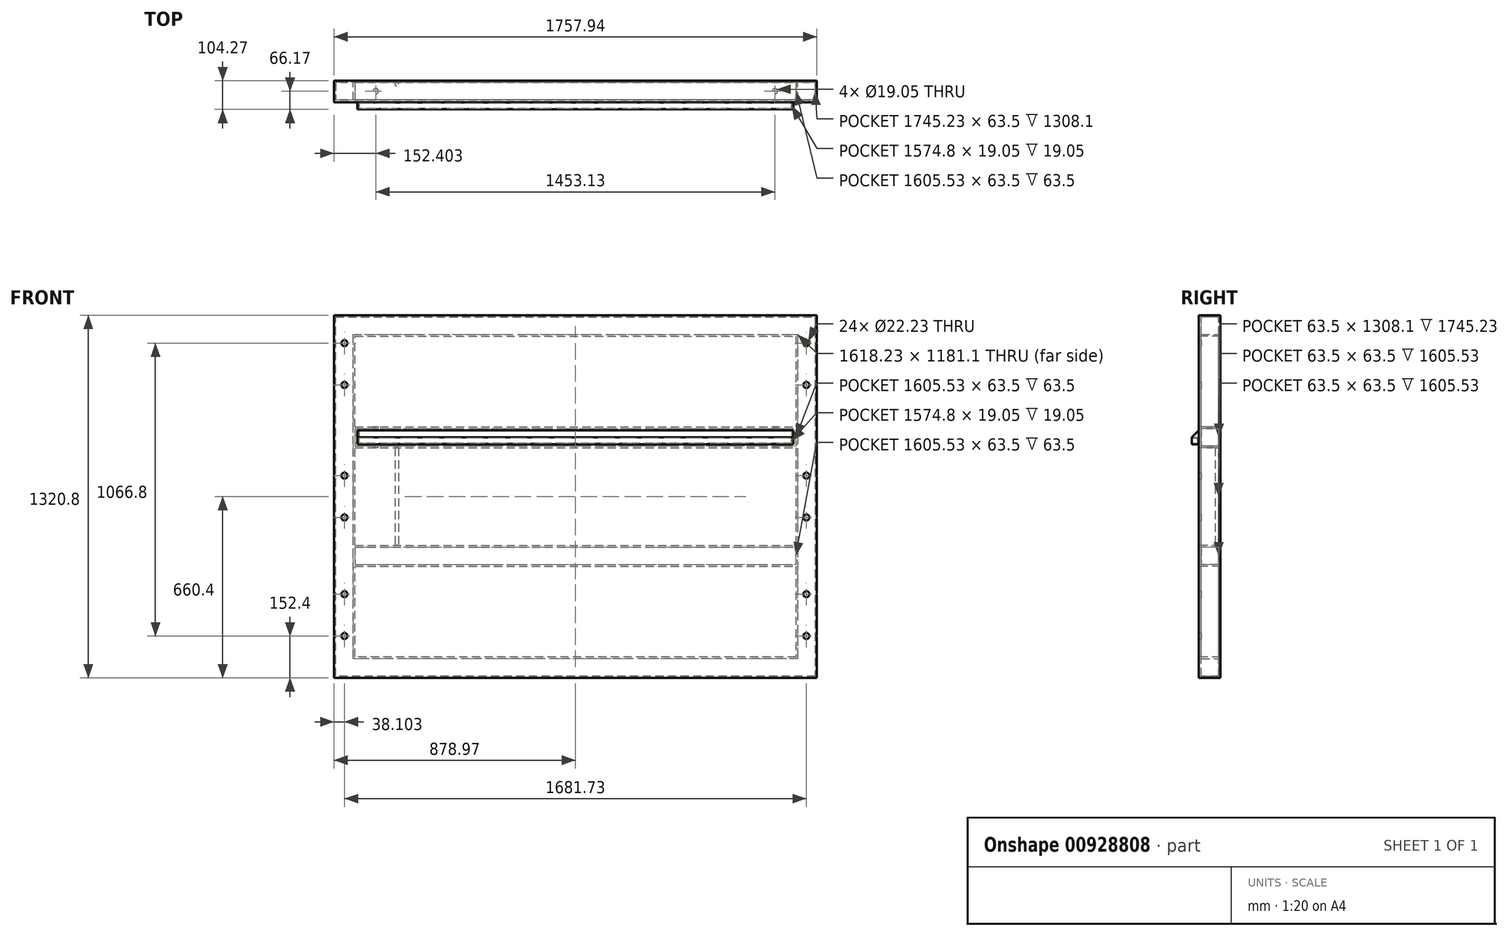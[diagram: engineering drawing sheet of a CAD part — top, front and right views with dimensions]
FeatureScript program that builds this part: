
annotation { "Feature Type Name" : "Feature", "Feature Type Description" : "" }
export const myFeature = defineFeature(function(context is Context, id is Id, definition is map)
    precondition{}
    {
        {
            var Q0;
            Q0=qCreatedBy(makeId("Front.planeOp"),FACE);
            var sketch = newSketch(context, id + "F0", { "sketchPlane" : qUnion([Q0])});
            skLineSegment(sketch, "E0.bottom", {"start": v(-878.97, 660.4) * mm, "end": v(878.97, 660.4) * mm});
            skLineSegment(sketch, "E0.top", {"start": v(-878.97, -660.4) * mm, "end": v(878.97, -660.4) * mm});
            skLineSegment(sketch, "E0.left", {"start": v(-878.97, 660.4) * mm, "end": v(-878.97, -660.4) * mm});
            skLineSegment(sketch, "E0.right", {"start": v(878.97, 660.4) * mm, "end": v(878.97, -660.4) * mm});
            skLineSegment(sketch, "E1.bottom", {"start": v(-802.77, 635) * mm, "end": v(802.77, 635) * mm, "construction": true});
            skLineSegment(sketch, "E1.top", {"start": v(-802.77, -609.6) * mm, "end": v(802.77, -609.6) * mm, "construction": true});
            skLineSegment(sketch, "E1.left", {"start": v(-802.77, 635) * mm, "end": v(-802.77, -609.6) * mm, "construction": true});
            skLineSegment(sketch, "E1.right", {"start": v(802.77, 635) * mm, "end": v(802.77, -609.6) * mm, "construction": true});
            skLineSegment(sketch, "E2", {"start": v(0, 0) * mm, "end": v(0, 635) * mm, "construction": true});
            skSolve(sketch);
        }
        {
            var Q0;
            Q0=qCreatedBy(makeId("Top.planeOp"),FACE);
            var sketch = newSketch(context, id + "F1", { "sketchPlane" : qUnion([Q0])});
            skLineSegment(sketch, "E3.bottom", {"start": v(-802.77, -76.2) * mm, "end": v(-878.97, -76.2) * mm});
            skLineSegment(sketch, "E3.top", {"start": v(-802.77, 0) * mm, "end": v(-878.97, 0) * mm});
            skLineSegment(sketch, "E3.left", {"start": v(-802.77, -76.2) * mm, "end": v(-802.77, 0) * mm});
            skLineSegment(sketch, "E3.right", {"start": v(-878.97, -76.2) * mm, "end": v(-878.97, 0) * mm});
            skPoint(sketch, "E3.middle", {"position": v(-840.87, -38.1) * mm});
            skLineSegment(sketch, "E4.bottom", {"start": v(-809.12, -69.85) * mm, "end": v(-872.62, -69.85) * mm});
            skLineSegment(sketch, "E4.top", {"start": v(-809.12, -6.35) * mm, "end": v(-872.62, -6.35) * mm});
            skLineSegment(sketch, "E4.left", {"start": v(-809.12, -69.85) * mm, "end": v(-809.12, -6.35) * mm});
            skLineSegment(sketch, "E4.right", {"start": v(-872.62, -69.85) * mm, "end": v(-872.62, -6.35) * mm});
            skSolve(sketch);
        }
        {
            var Q0;
            Q0=qSketchRegion(id+"F1",true);
            var Q1;
            Q1=qConstructionFilter(qBodyType(qCreatedBy(id+"F0",EDGE),BodyType.WIRE),ConstructionObject.NO);
            sweep(context, id + "F2", {"profiles" : qUnion([Q0]), "path" : qUnion([Q1])});
        }
        {
            var Q0;
            Q0=qCreatedBy(makeId("Right.planeOp"),FACE);
            var sketch = newSketch(context, id + "F3", { "sketchPlane" : qUnion([Q0])});
            skLineSegment(sketch, "E5.bottom", {"start": v(0, 660.4) * mm, "end": v(-76.2, 660.4) * mm, "construction": true});
            skLineSegment(sketch, "E5.top", {"start": v(0, 584.2) * mm, "end": v(-76.2, 584.2) * mm, "construction": true});
            skLineSegment(sketch, "E5.left", {"start": v(0, 660.4) * mm, "end": v(0, 584.2) * mm, "construction": true});
            skLineSegment(sketch, "E5.right", {"start": v(-76.2, 660.4) * mm, "end": v(-76.2, 584.2) * mm, "construction": true});
            skPoint(sketch, "E5.middle", {"position": v(-38.1, 622.3) * mm});
            skLineSegment(sketch, "E6.bottom", {"start": v(-6.35, 654.05) * mm, "end": v(-69.85, 654.05) * mm, "construction": true});
            skLineSegment(sketch, "E6.top", {"start": v(-6.35, 590.55) * mm, "end": v(-69.85, 590.55) * mm, "construction": true});
            skLineSegment(sketch, "E6.left", {"start": v(-6.35, 654.05) * mm, "end": v(-6.35, 590.55) * mm, "construction": true});
            skLineSegment(sketch, "E6.right", {"start": v(-69.85, 654.05) * mm, "end": v(-69.85, 590.55) * mm, "construction": true});
            skLineSegment(sketch, "E7.0.1.0", {"start": v(0, 254) * mm, "end": v(-76.2, 254) * mm});
            skLineSegment(sketch, "E7.0.1.1", {"start": v(0, 177.8) * mm, "end": v(-76.2, 177.8) * mm});
            skLineSegment(sketch, "E7.0.1.2", {"start": v(0, 254) * mm, "end": v(0, 177.8) * mm});
            skLineSegment(sketch, "E7.0.1.3", {"start": v(-76.2, 254) * mm, "end": v(-76.2, 177.8) * mm});
            skLineSegment(sketch, "E7.0.1.4", {"start": v(-6.35, 247.65) * mm, "end": v(-69.85, 247.65) * mm});
            skLineSegment(sketch, "E7.0.1.5", {"start": v(-6.35, 184.15) * mm, "end": v(-69.85, 184.15) * mm});
            skLineSegment(sketch, "E7.0.1.6", {"start": v(-6.35, 247.65) * mm, "end": v(-6.35, 184.15) * mm});
            skLineSegment(sketch, "E7.0.1.7", {"start": v(-69.85, 247.65) * mm, "end": v(-69.85, 184.15) * mm});
            skLineSegment(sketch, "E7.direction1", {"start": v(-76.2, 584.2) * mm, "end": v(586.54, 584.2) * mm, "construction": true});
            skLineSegment(sketch, "E8.0.0.2", {"start": v(0, -177.8) * mm, "end": v(-76.2, -177.8) * mm});
            skLineSegment(sketch, "E8.3.0.2", {"start": v(0, -254) * mm, "end": v(-76.2, -254) * mm});
            skLineSegment(sketch, "E8.6.0.2", {"start": v(0, -177.8) * mm, "end": v(0, -254) * mm});
            skLineSegment(sketch, "E8.9.0.2", {"start": v(-76.2, -177.8) * mm, "end": v(-76.2, -254) * mm});
            skLineSegment(sketch, "E8.12.0.2", {"start": v(-6.35, -184.15) * mm, "end": v(-69.85, -184.15) * mm});
            skLineSegment(sketch, "E8.15.0.2", {"start": v(-6.35, -247.65) * mm, "end": v(-69.85, -247.65) * mm});
            skLineSegment(sketch, "E8.18.0.2", {"start": v(-6.35, -184.15) * mm, "end": v(-6.35, -247.65) * mm});
            skLineSegment(sketch, "E8.21.0.2", {"start": v(-69.85, -184.15) * mm, "end": v(-69.85, -247.65) * mm});
            skLineSegment(sketch, "E9", {"start": v(-38.1, 584.2) * mm, "end": v(-38.1, 254) * mm, "construction": true});
            skLineSegment(sketch, "E10", {"start": v(-38.1, 177.8) * mm, "end": v(-38.1, -177.8) * mm, "construction": true});
            skLineSegment(sketch, "E11", {"start": v(-38.1, -254) * mm, "end": v(-38.1, -584.2) * mm, "construction": true});
            skLineSegment(sketch, "E12", {"start": v(-38.1, 254) * mm, "end": v(-38.1, 247.65) * mm, "construction": true});
            skLineSegment(sketch, "E13", {"start": v(-69.85, 215.9) * mm, "end": v(-76.2, 215.9) * mm, "construction": true});
            skPoint(sketch, "E13.endSnap0", {"position": v(-76.2, 215.9) * mm});
            skLineSegment(sketch, "E14", {"start": v(-38.1, -254) * mm, "end": v(-38.1, -247.65) * mm, "construction": true});
            skLineSegment(sketch, "E15", {"start": v(-69.85, -215.9) * mm, "end": v(-76.2, -215.9) * mm, "construction": true});
            skSolve(sketch);
        }
        {
            var Q0;
            Q0=qSketchRegion(id+"F3",true);
            var Q1;
            Q1=makeQuery(id+"F2.opSweep","SWEPT_FACE",FACE,{"disambiguationData":[OSD([sQuery(id+"F0.wireOp",EDGE,"E0.left"),sQuery(id+"F1.wireOp",EDGE,"E3.left")])]});
            var Q2;
            Q2=makeQuery(id+"F2.opSweep","CAP_VERTEX",VERTEX,{"disambiguationData":[OSD([sQuery(id+"F0.wireOp",EDGE,"E0.bottom"),sQuery(id+"F1.wireOp",EDGE,"E3.bottom"),sQuery(id+"F1.wireOp",EDGE,"E3.left")])],"isStart":true});
            var Q3;
            Q3=makeQuery(id+"F2.opSweep","SWEPT_FACE",FACE,{"disambiguationData":[OSD([sQuery(id+"F0.wireOp",EDGE,"E0.right"),sQuery(id+"F1.wireOp",EDGE,"E3.left")])]});
            var Q4;
            Q4=makeQuery(id+"F2.opSweep","MID_CAP_VERTEX",VERTEX,{"disambiguationData":[OSD([sQuery(id+"F0.wireOp",EDGE,"E0.bottom"),sQuery(id+"F1.wireOp",EDGE,"E3.bottom"),sQuery(id+"F1.wireOp",EDGE,"E3.left")])],"capPos":1.0});
            extrude(context, id + "F4", {"entities" : qUnion([Q0]), "operationType" : NewBodyOperationType.ADD, "endBound" : BoundingType.UP_TO_VERTEX, "oppositeDirection" : true, "depth" : 25.4 * mm, "endBoundEntityFace" : qUnion([Q1]), "endBoundEntityVertex" : qUnion([Q2]), "offsetDistance" : 25.4 * mm, "hasSecondDirection" : true, "secondDirectionBound" : SecondDirectionBoundingType.UP_TO_VERTEX, "secondDirectionOppositeDirection" : false, "secondDirectionDepth" : 25.4 * mm, "secondDirectionBoundEntityFace" : qUnion([Q3]), "secondDirectionBoundEntityVertex" : qUnion([Q4])});
        }
        {
            var Q0;
            Q0=qCreatedBy(makeId("Top.planeOp"),FACE);
            var sketch = newSketch(context, id + "F5", { "sketchPlane" : qUnion([Q0])});
            skLineSegment(sketch, "E16.bottom", {"start": v(878.97, -78.87) * mm, "end": v(-878.97, -78.87) * mm});
            skLineSegment(sketch, "E16.top", {"start": v(878.97, -76.2) * mm, "end": v(-878.97, -76.2) * mm});
            skLineSegment(sketch, "E16.left", {"start": v(878.97, -78.87) * mm, "end": v(878.97, -76.2) * mm});
            skLineSegment(sketch, "E16.right", {"start": v(-878.97, -78.87) * mm, "end": v(-878.97, -76.2) * mm});
            skPoint(sketch, "E16.middle", {"position": v(0, -77.53) * mm});
            skSolve(sketch);
        }
        {
            var Q0;
            Q0=qSketchRegion(id+"F5",true);
            var Q1;
            Q1=makeQuery(id+"F2.opSweep","CAP_VERTEX",VERTEX,{"disambiguationData":[OSD([sQuery(id+"F0.wireOp",EDGE,"E0.bottom"),sQuery(id+"F1.wireOp",EDGE,"E3.bottom"),sQuery(id+"F1.wireOp",EDGE,"E3.right")])],"isStart":true});
            var Q2;
            Q2=makeQuery(id+"F2.opSweep","MID_CAP_VERTEX",VERTEX,{"disambiguationData":[OSD([sQuery(id+"F0.wireOp",EDGE,"E0.left"),sQuery(id+"F1.wireOp",EDGE,"E3.bottom"),sQuery(id+"F1.wireOp",EDGE,"E3.right")])],"capPos":3.0});
            extrude(context, id + "F6", {"entities" : qUnion([Q0]), "operationType" : NewBodyOperationType.ADD, "endBound" : BoundingType.UP_TO_VERTEX, "depth" : 25.4 * mm, "endBoundEntityVertex" : qUnion([Q1]), "offsetDistance" : 25.4 * mm, "hasSecondDirection" : true, "secondDirectionBound" : SecondDirectionBoundingType.UP_TO_VERTEX, "secondDirectionOppositeDirection" : true, "secondDirectionDepth" : 25.4 * mm, "secondDirectionBoundEntityVertex" : qUnion([Q2])});
        }
        {
            var Q0;
            Q0=qCreatedBy(makeId("Right.planeOp"),FACE);
            var sketch = newSketch(context, id + "F7", { "sketchPlane" : qUnion([Q0])});
            skLineSegment(sketch, "E17.bottom", {"start": v(-78.87, 215.9) * mm, "end": v(-104.27, 215.9) * mm});
            skLineSegment(sketch, "E17.top", {"start": v(-78.87, 190.5) * mm, "end": v(-104.27, 190.5) * mm});
            skLineSegment(sketch, "E17.left", {"start": v(-78.87, 215.9) * mm, "end": v(-78.87, 190.5) * mm});
            skLineSegment(sketch, "E17.right", {"start": v(-104.27, 215.9) * mm, "end": v(-104.27, 190.5) * mm});
            skPoint(sketch, "E17.middle", {"position": v(-91.57, 203.2) * mm});
            skLineSegment(sketch, "E18.bottom", {"start": v(-82.04, 212.73) * mm, "end": v(-101.1, 212.73) * mm});
            skLineSegment(sketch, "E18.top", {"start": v(-82.04, 193.68) * mm, "end": v(-101.1, 193.68) * mm});
            skLineSegment(sketch, "E18.left", {"start": v(-82.04, 212.73) * mm, "end": v(-82.04, 193.68) * mm});
            skLineSegment(sketch, "E18.right", {"start": v(-101.1, 212.73) * mm, "end": v(-101.1, 193.68) * mm});
            skLineSegment(sketch, "E19", {"start": v(-104.27, 215.9) * mm, "end": v(-78.87, 241.3) * mm});
            skPoint(sketch, "E19.endSnap0", {"position": v(-78.87, 203.2) * mm});
            skLineSegment(sketch, "E20", {"start": v(-78.87, 241.3) * mm, "end": v(-78.87, 215.9) * mm, "construction": true});
            skLineSegment(sketch, "E21", {"start": v(-78.87, 239.58) * mm, "end": v(-102.55, 215.9) * mm});
            skLineSegment(sketch, "E22", {"start": v(-78.87, 239.58) * mm, "end": v(-78.87, 241.3) * mm});
            skSolve(sketch);
        }
        {
            var Q0;
            Q0=qSketchRegion(id+"F7",true);
            extrude(context, id + "F8", {"entities" : qUnion([Q0]), "operationType" : NewBodyOperationType.ADD, "endBound" : BoundingType.SYMMETRIC, "depth" : 1587.5 * mm, "offsetDistance" : 25.4 * mm});
        }
        {
            var Q0;
            Q0=makeQuery(id+"F8.opExtrude","SWEPT_FACE",FACE,{"disambiguationData":[OSD([sQuery(id+"F7.wireOp",EDGE,"E17.top")])]});
            var sketch = newSketch(context, id + "F9", { "sketchPlane" : qUnion([Q0])});
            skLineSegment(sketch, "E23.bottom", {"start": v(793.75, 78.87) * mm, "end": v(787.4, 78.87) * mm});
            skLineSegment(sketch, "E23.top", {"start": v(793.75, 104.27) * mm, "end": v(787.4, 104.27) * mm});
            skLineSegment(sketch, "E23.left", {"start": v(793.75, 104.27) * mm, "end": v(793.75, 78.87) * mm});
            skLineSegment(sketch, "E23.right", {"start": v(787.4, 104.27) * mm, "end": v(787.4, 78.87) * mm});
            skLineSegment(sketch, "E24.bottom", {"start": v(-793.75, 78.87) * mm, "end": v(-787.4, 78.87) * mm});
            skLineSegment(sketch, "E24.top", {"start": v(-793.75, 104.27) * mm, "end": v(-787.4, 104.27) * mm});
            skLineSegment(sketch, "E24.left", {"start": v(-793.75, 104.27) * mm, "end": v(-793.75, 78.87) * mm});
            skLineSegment(sketch, "E24.right", {"start": v(-787.4, 104.27) * mm, "end": v(-787.4, 78.87) * mm});
            skSolve(sketch);
        }
        {
            var Q0;
            Q0=qSketchRegion(id+"F9",true);
            var Q1;
            Q1=makeQuery(id+"F8.opExtrude","SWEPT_FACE",FACE,{"disambiguationData":[OSD([sQuery(id+"F7.wireOp",EDGE,"E21")])]});
            var Q2;
            Q2=makeQuery(id+"F8.opExtrude","CAP_VERTEX",VERTEX,{"disambiguationData":[OSD([sQuery(id+"F7.wireOp",EDGE,"E17.top"),sQuery(id+"F7.wireOp",EDGE,"E17.right")])],"isStart":false});
            extrude(context, id + "F10", {"entities" : qUnion([Q0]), "operationType" : NewBodyOperationType.ADD, "endBound" : BoundingType.UP_TO_SURFACE, "oppositeDirection" : true, "depth" : 25.4 * mm, "endBoundEntityFace" : qUnion([Q1]), "endBoundEntityVertex" : qUnion([Q2]), "offsetDistance" : 25.4 * mm});
        }
        {
            var Q0;
            Q0=qCreatedBy(makeId("Front.planeOp"),FACE);
            var sketch = newSketch(context, id + "F11", { "sketchPlane" : qUnion([Q0])});
            skCircle(sketch, "E25", {"center": v(-840.87, -76.2) * mm, "radius": 11.11 * mm});
            skCircle(sketch, "E26", {"center": v(-840.87, -508) * mm, "radius": 11.11 * mm});
            skCircle(sketch, "E27", {"center": v(-840.87, 76.2) * mm, "radius": 11.11 * mm});
            skCircle(sketch, "E28", {"center": v(-840.87, -355.6) * mm, "radius": 11.11 * mm});
            skLineSegment(sketch, "E29", {"start": v(-840.87, 76.2) * mm, "end": v(-840.87, -76.2) * mm, "construction": true});
            skLineSegment(sketch, "E30", {"start": v(-840.87, -355.6) * mm, "end": v(-840.87, -508) * mm, "construction": true});
            skCircle(sketch, "E31", {"center": v(-840.87, 406.4) * mm, "radius": 11.11 * mm});
            skCircle(sketch, "E32", {"center": v(-840.87, 558.8) * mm, "radius": 11.11 * mm});
            skLineSegment(sketch, "E33", {"start": v(-840.87, 558.8) * mm, "end": v(-840.87, 406.4) * mm, "construction": true});
            skLineSegment(sketch, "E34", {"start": v(-840.87, -660.4) * mm, "end": v(-840.87, -584.2) * mm, "construction": true});
            skLineSegment(sketch, "E35", {"start": v(-840.87, -584.2) * mm, "end": v(-840.87, -279.4) * mm, "construction": true});
            skLineSegment(sketch, "E36", {"start": v(-840.87, -279.4) * mm, "end": v(-840.87, -177.8) * mm, "construction": true});
            skLineSegment(sketch, "E37", {"start": v(-840.87, -177.8) * mm, "end": v(-840.87, 177.8) * mm, "construction": true});
            skLineSegment(sketch, "E38", {"start": v(-840.87, 177.8) * mm, "end": v(-840.87, 381) * mm, "construction": true});
            skLineSegment(sketch, "E39", {"start": v(-840.87, 381) * mm, "end": v(-840.87, 584.2) * mm, "construction": true});
            skLineSegment(sketch, "E40", {"start": v(-840.87, 660.4) * mm, "end": v(-840.87, 584.2) * mm, "construction": true});
            skLineSegment(sketch, "E41", {"start": v(-840.87, -660.4) * mm, "end": v(-840.87, -685.8) * mm, "construction": true});
            skPoint(sketch, "E42", {"position": v(-840.87, 482.6) * mm});
            skPoint(sketch, "E43", {"position": v(-840.87, 0) * mm});
            skPoint(sketch, "E44", {"position": v(-840.87, -431.8) * mm});
            skLineSegment(sketch, "E45", {"start": v(0, 0) * mm, "end": v(0, 742.9) * mm, "construction": true});
            skCircle(sketch, "E46.MirrorC", {"center": v(840.87, 558.8) * mm, "radius": 11.11 * mm});
            skCircle(sketch, "E47.MirrorC", {"center": v(840.87, 406.4) * mm, "radius": 11.11 * mm});
            skCircle(sketch, "E48.MirrorC", {"center": v(840.87, 76.2) * mm, "radius": 11.11 * mm});
            skCircle(sketch, "E49.MirrorC", {"center": v(840.87, -76.2) * mm, "radius": 11.11 * mm});
            skCircle(sketch, "E50.MirrorC", {"center": v(840.87, -355.6) * mm, "radius": 11.11 * mm});
            skCircle(sketch, "E51.MirrorC", {"center": v(840.87, -508) * mm, "radius": 11.11 * mm});
            skSolve(sketch);
        }
        {
            var Q0;
            Q0=qSketchRegion(id+"F11",true);
            extrude(context, id + "F12", {"entities" : qUnion([Q0]), "operationType" : NewBodyOperationType.REMOVE, "endBound" : BoundingType.THROUGH_ALL, "depth" : 25.4 * mm, "offsetDistance" : 25.4 * mm});
        }
        {
            var Q0;
            Q0=makeQuery(id+"F4.opExtrude","SWEPT_FACE",FACE,{"disambiguationData":[OSD([sQuery(id+"F3.wireOp",EDGE,"E7.0.1.0")])]});
            var sketch = newSketch(context, id + "F13", { "sketchPlane" : qUnion([Q0])});
            skCircle(sketch, "E52", {"center": v(-726.57, -38.1) * mm, "radius": 9.53 * mm});
            skLineSegment(sketch, "E53", {"start": v(-726.57, -38.1) * mm, "end": v(0, -38.1) * mm, "construction": true});
            skLineSegment(sketch, "E54", {"start": v(-726.57, -764.67) * mm, "end": v(-726.57, -38.1) * mm, "construction": true});
            skLineSegment(sketch, "E55", {"start": v(-726.57, 60.36) * mm, "end": v(-726.57, -38.1) * mm, "construction": true});
            skLineSegment(sketch, "E56", {"start": v(-726.57, 0) * mm, "end": v(-726.57, -38.1) * mm, "construction": true});
            skLineSegment(sketch, "E57", {"start": v(-802.77, 0) * mm, "end": v(-726.57, 0) * mm, "construction": true});
            skLineSegment(sketch, "E58", {"start": v(0, -76.2) * mm, "end": v(0, 0) * mm, "construction": true});
            skCircle(sketch, "E59.MirrorC", {"center": v(726.57, -38.1) * mm, "radius": 9.53 * mm});
            skSolve(sketch);
        }
        {
            var Q0;
            Q0=qSketchRegion(id+"F13",true);
            var Q1;
            Q1=makeQuery(id+"F4.opExtrude","SWEPT_FACE",FACE,{"disambiguationData":[OSD([sQuery(id+"F3.wireOp",EDGE,"E7.0.1.1")])]});
            extrude(context, id + "F14", {"entities" : qUnion([Q0]), "operationType" : NewBodyOperationType.REMOVE, "endBound" : BoundingType.UP_TO_SURFACE, "oppositeDirection" : true, "depth" : 25.4 * mm, "endBoundEntityFace" : qUnion([Q1]), "offsetDistance" : 25.4 * mm});
        }
        {
            var Q0;
            Q0=qCreatedBy(makeId("Top.planeOp"),FACE);
            var sketch = newSketch(context, id + "F15", { "sketchPlane" : qUnion([Q0])});
            skCircle(sketch, "E60", {"center": v(-650.37, -12.7) * mm, "radius": 6.35 * mm});
            skLineSegment(sketch, "E61", {"start": v(-650.37, -12.7) * mm, "end": v(-650.37, -76.2) * mm, "construction": true});
            skLineSegment(sketch, "E62", {"start": v(-650.37, 0) * mm, "end": v(-650.37, -12.7) * mm, "construction": true});
            skSolve(sketch);
        }
        {
            var Q0;
            Q0=qSketchRegion(id+"F15",true);
            extrude(context, id + "F16", {"entities" : qUnion([Q0]), "operationType" : NewBodyOperationType.ADD, "endBound" : BoundingType.UP_TO_NEXT, "depth" : 25.4 * mm, "offsetDistance" : 25.4 * mm, "hasSecondDirection" : true, "secondDirectionBound" : SecondDirectionBoundingType.UP_TO_NEXT, "secondDirectionOppositeDirection" : true, "secondDirectionDepth" : 25.4 * mm});
        }
    });
